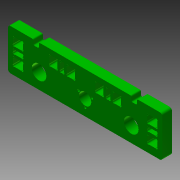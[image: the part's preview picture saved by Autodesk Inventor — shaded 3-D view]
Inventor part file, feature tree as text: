
AUTODESK INVENTOR PART (.ipt)
format: ipt  version: 2012 SP1 (Build 160190100, 190)  size: 270,336 bytes
history: native  units: in
note: dims shown in document units (in); Inventor stores cm internally (conversion verified against a paired STEP export)
features: other x4, extrude x2
ambient origin geometry x8: Origin, YZ Plane, XZ Plane, XY Plane, X Axis, Y Axis, Z Axis, Center Point
bodies: Solid1 (feature_tree)
feature tree (6):
  other  "skeleton.ipt"
  other  "DRILL-THROUGH"
  other  "STOCK_12MM"
  extrude  "Extrusion1"  Depth=0.3937in
  extrude  "Extrusion2"  Depth=0.4724in
  other  "THROUGH-CUT"
